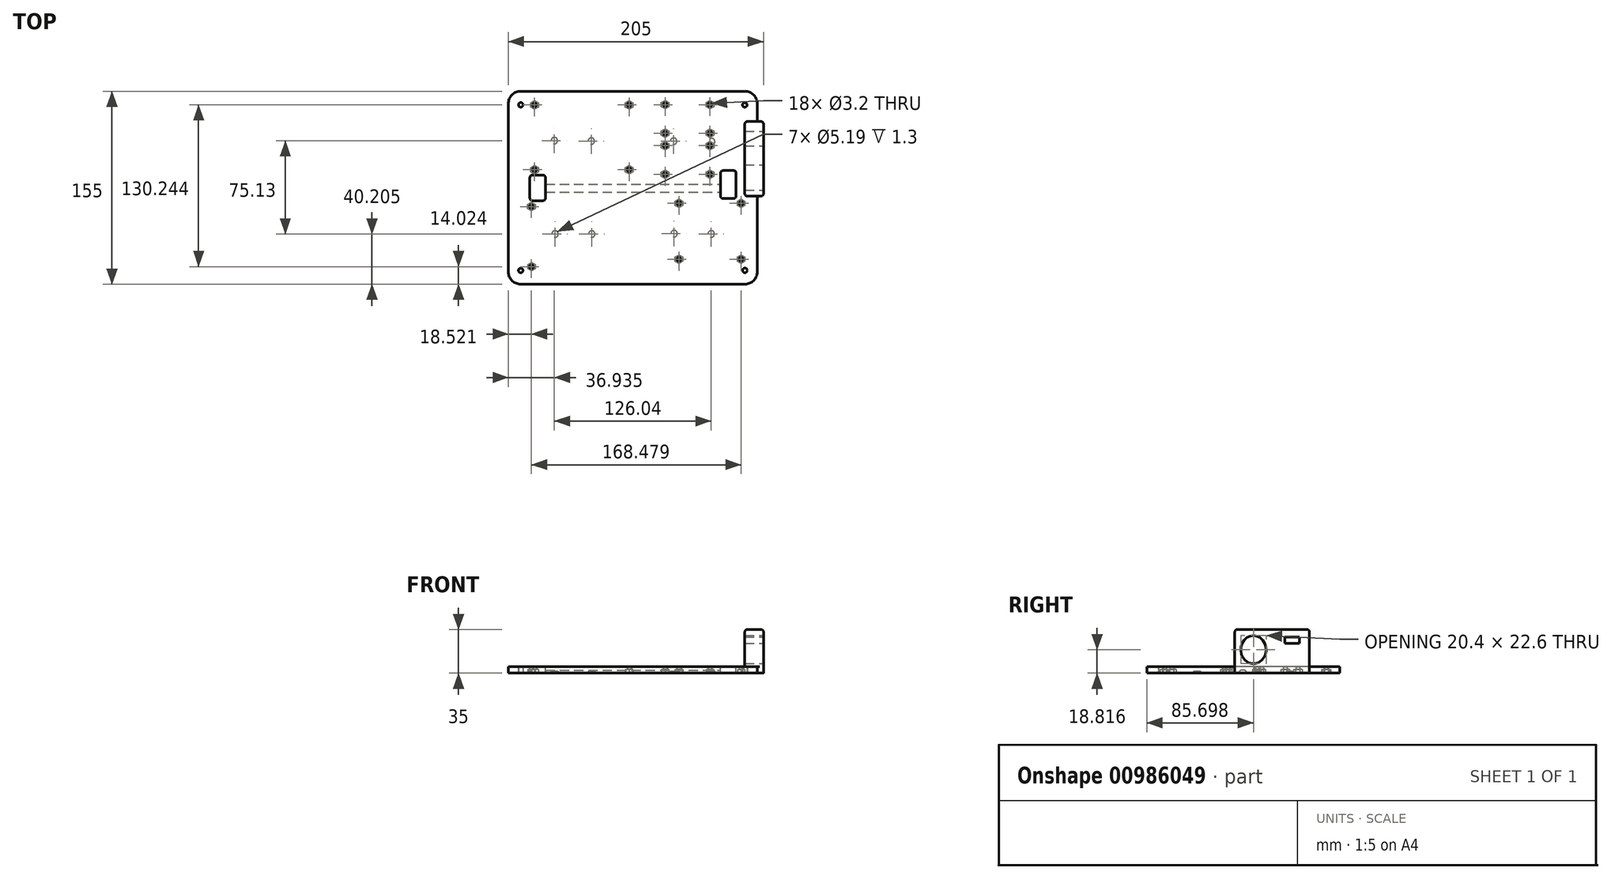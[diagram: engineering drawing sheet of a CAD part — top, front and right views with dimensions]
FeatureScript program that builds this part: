
annotation { "Feature Type Name" : "Feature", "Feature Type Description" : "" }
export const myFeature = defineFeature(function(context is Context, id is Id, definition is map)
    precondition{}
    {
        {
            var Q0;
            Q0=qCreatedBy(makeId("Top.planeOp"),FACE);
            var sketch = newSketch(context, id + "F0", { "sketchPlane" : qUnion([Q0])});
            skLineSegment(sketch, "E0.bottom", {"start": v(90, 77.5) * mm, "end": v(-90, 77.5) * mm});
            skLineSegment(sketch, "E0.top", {"start": v(90, -77.5) * mm, "end": v(-90, -77.5) * mm});
            skLineSegment(sketch, "E0.left", {"start": v(100, 67.5) * mm, "end": v(100, -67.5) * mm});
            skLineSegment(sketch, "E0.right", {"start": v(-100, 67.5) * mm, "end": v(-100, -67.5) * mm});
            skPoint(sketch, "E0.middle", {"position": v(0, 0) * mm});
            skPoint(sketch, "E1.visualSharp", {"position": v(-100, 77.5) * mm});
            skArc(sketch, "E1.filletArc", {"start": v(-90, 77.5) * mm, "mid": v(-97.07, 74.57) * mm, "end": v(-100, 67.5) * mm});
            skPoint(sketch, "E2.visualSharp", {"position": v(-100, -77.5) * mm});
            skArc(sketch, "E2.filletArc", {"start": v(-100, -67.5) * mm, "mid": v(-97.07, -74.57) * mm, "end": v(-90, -77.5) * mm});
            skPoint(sketch, "E3.visualSharp", {"position": v(100, -77.5) * mm});
            skArc(sketch, "E3.filletArc", {"start": v(90, -77.5) * mm, "mid": v(97.07, -74.57) * mm, "end": v(100, -67.5) * mm});
            skPoint(sketch, "E4.visualSharp", {"position": v(100, 77.5) * mm});
            skArc(sketch, "E4.filletArc", {"start": v(100, 67.5) * mm, "mid": v(97.07, 74.57) * mm, "end": v(90, 77.5) * mm});
            skSolve(sketch);
        }
        {
            var Q0;
            Q0=makeQuery(id+"F0.imprint","IMPRINT",FACE,{"disambiguationData":[TD([[makeQuery(id+"F0.imprint","IMPRINT",EDGE,{"derivedFrom":sQuery(id+"F0.wireOp",EDGE,"E0.bottom")}),1.0]])]});
            extrude(context, id + "F1", {"entities" : qUnion([Q0]), "depth" : 5 * mm, "offsetDistance" : 25 * mm});
        }
        {
            var Q0;
            Q0=qCreatedBy(makeId("Top.planeOp"),FACE);
            var sketch = newSketch(context, id + "F2", { "sketchPlane" : qUnion([Q0])});
            skCircle(sketch, "E5", {"center": v(-90.08, -66.5) * mm, "radius": 1.85 * mm});
            skCircle(sketch, "E6", {"center": v(90.07, -66.42) * mm, "radius": 1.85 * mm});
            skCircle(sketch, "E7", {"center": v(-90.05, 66.58) * mm, "radius": 1.85 * mm});
            skCircle(sketch, "E8", {"center": v(89.94, 66.51) * mm, "radius": 1.85 * mm});
            skCircle(sketch, "E9", {"center": v(-62.46, -37.16) * mm, "radius": 2.6 * mm});
            skCircle(sketch, "E10", {"center": v(-63.07, 37.84) * mm, "radius": 2.6 * mm});
            skCircle(sketch, "E11", {"center": v(-33.39, 37.49) * mm, "radius": 2.6 * mm});
            skCircle(sketch, "E12", {"center": v(32.78, 37.34) * mm, "radius": 2.6 * mm});
            skCircle(sketch, "E13", {"center": v(62.98, -37.14) * mm, "radius": 2.6 * mm});
            skCircle(sketch, "E14", {"center": v(33.16, -36.9) * mm, "radius": 2.6 * mm});
            skCircle(sketch, "E15", {"center": v(-32.97, -37.3) * mm, "radius": 2.6 * mm});
            skCircle(sketch, "E16", {"center": v(63.34, 37) * mm, "radius": 2.6 * mm});
            skLineSegment(sketch, "E17.bottom", {"start": v(-79.95, -3.5) * mm, "end": v(80.05, -3.5) * mm});
            skLineSegment(sketch, "E17.top", {"start": v(-79.95, 2.7) * mm, "end": v(80.05, 2.7) * mm});
            skLineSegment(sketch, "E17.left", {"start": v(-79.95, -3.5) * mm, "end": v(-79.95, 2.7) * mm});
            skLineSegment(sketch, "E17.right", {"start": v(80.05, -3.5) * mm, "end": v(80.05, 2.7) * mm});
            skLineSegment(sketch, "E18", {"start": v(-10.82, -3.5) * mm, "end": v(-10.82, -77.5) * mm});
            skLineSegment(sketch, "E19", {"start": v(-79.95, -1.61) * mm, "end": v(-99.95, -1.61) * mm});
            skSolve(sketch);
        }
        {
            var Q0;
            Q0=makeQuery(id+"F2.imprint","IMPRINT",FACE,{"disambiguationData":[TD([[makeQuery(id+"F2.imprint","IMPRINT",EDGE,{"derivedFrom":sQuery(id+"F2.wireOp",EDGE,"E5")}),1.0]])]});
            var Q1;
            Q1=makeQuery(id+"F2.imprint","IMPRINT",FACE,{"disambiguationData":[TD([[makeQuery(id+"F2.imprint","IMPRINT",EDGE,{"derivedFrom":sQuery(id+"F2.wireOp",EDGE,"E6")}),1.0]])]});
            var Q2;
            Q2=makeQuery(id+"F2.imprint","IMPRINT",FACE,{"disambiguationData":[TD([[makeQuery(id+"F2.imprint","IMPRINT",EDGE,{"derivedFrom":sQuery(id+"F2.wireOp",EDGE,"E7")}),1.0]])]});
            var Q3;
            Q3=makeQuery(id+"F2.imprint","IMPRINT",FACE,{"disambiguationData":[TD([[makeQuery(id+"F2.imprint","IMPRINT",EDGE,{"derivedFrom":sQuery(id+"F2.wireOp",EDGE,"E8")}),1.0]])]});
            extrude(context, id + "F3", {"entities" : qUnion([Q0, Q1, Q2, Q3]), "operationType" : NewBodyOperationType.REMOVE, "depth" : 5 * mm, "offsetDistance" : 25 * mm});
        }
        {
            var Q0;
            Q0=makeQuery(id+"F2.imprint","IMPRINT",FACE,{"disambiguationData":[TD([[makeQuery(id+"F2.imprint","IMPRINT",EDGE,{"derivedFrom":sQuery(id+"F2.wireOp",EDGE,"E9")}),1.0]])]});
            var Q1;
            Q1=makeQuery(id+"F2.imprint","IMPRINT",FACE,{"disambiguationData":[TD([[makeQuery(id+"F2.imprint","IMPRINT",EDGE,{"derivedFrom":sQuery(id+"F2.wireOp",EDGE,"E15")}),1.0]])]});
            var Q2;
            Q2=makeQuery(id+"F2.imprint","IMPRINT",FACE,{"disambiguationData":[TD([[makeQuery(id+"F2.imprint","IMPRINT",EDGE,{"derivedFrom":sQuery(id+"F2.wireOp",EDGE,"E14")}),1.0]])]});
            var Q3;
            Q3=makeQuery(id+"F2.imprint","IMPRINT",FACE,{"disambiguationData":[TD([[makeQuery(id+"F2.imprint","IMPRINT",EDGE,{"derivedFrom":sQuery(id+"F2.wireOp",EDGE,"E13")}),1.0]])]});
            var Q4;
            Q4=makeQuery(id+"F2.imprint","IMPRINT",FACE,{"disambiguationData":[TD([[makeQuery(id+"F2.imprint","IMPRINT",EDGE,{"derivedFrom":sQuery(id+"F2.wireOp",EDGE,"E16")}),1.0]])]});
            var Q5;
            Q5=makeQuery(id+"F2.imprint","IMPRINT",FACE,{"disambiguationData":[TD([[makeQuery(id+"F2.imprint","IMPRINT",EDGE,{"derivedFrom":sQuery(id+"F2.wireOp",EDGE,"E12")}),1.0]])]});
            var Q6;
            Q6=makeQuery(id+"F2.imprint","IMPRINT",FACE,{"disambiguationData":[TD([[makeQuery(id+"F2.imprint","IMPRINT",EDGE,{"derivedFrom":sQuery(id+"F2.wireOp",EDGE,"E11")}),1.0]])]});
            var Q7;
            Q7=makeQuery(id+"F2.imprint","IMPRINT",FACE,{"disambiguationData":[TD([[makeQuery(id+"F2.imprint","IMPRINT",EDGE,{"derivedFrom":sQuery(id+"F2.wireOp",EDGE,"E10")}),1.0]])]});
            extrude(context, id + "F4", {"entities" : qUnion([Q0, Q1, Q2, Q3, Q4, Q5, Q6, Q7]), "operationType" : NewBodyOperationType.REMOVE, "depth" : 1.3 * mm, "offsetDistance" : 25 * mm});
        }
        {
            var Q0;
            Q0=makeQuery(id+"F2.imprint","IMPRINT",FACE,{"disambiguationData":[TD([[makeQuery(id+"F2.imprint","IMPRINT",EDGE,{"derivedFrom":sQuery(id+"F2.wireOp",EDGE,"E17.bottom")}),1.0]])]});
            extrude(context, id + "F5", {"entities" : qUnion([Q0]), "operationType" : NewBodyOperationType.REMOVE, "depth" : 2.17 * mm, "offsetDistance" : 25 * mm});
        }
        {
            var Q0;
            Q0=qCreatedBy(makeId("Top.planeOp"),FACE);
            var sketch = newSketch(context, id + "F6", { "sketchPlane" : qUnion([Q0])});
            skCircle(sketch, "E20.cCircle", {"center": v(37, -57.5) * mm, "radius": 3 * mm, "construction": true});
            skLineSegment(sketch, "E20.0", {"start": v(40, -55.77) * mm, "end": v(40, -59.23) * mm});
            skLineSegment(sketch, "E20.1", {"start": v(40, -59.23) * mm, "end": v(37, -60.96) * mm});
            skLineSegment(sketch, "E20.2", {"start": v(37, -60.96) * mm, "end": v(34, -59.23) * mm});
            skLineSegment(sketch, "E20.3", {"start": v(34, -59.23) * mm, "end": v(34, -55.77) * mm});
            skLineSegment(sketch, "E20.4", {"start": v(34, -55.77) * mm, "end": v(37, -54.04) * mm});
            skLineSegment(sketch, "E20.5", {"start": v(37, -54.04) * mm, "end": v(40, -55.77) * mm});
            skPoint(sketch, "E20.0.midPoint", {"position": v(40, -57.5) * mm});
            skCircle(sketch, "E21", {"center": v(37, -57.5) * mm, "radius": 1.6 * mm});
            skCircle(sketch, "E22.0.1.0", {"center": v(37, -12.5) * mm, "radius": 1.6 * mm});
            skLineSegment(sketch, "E22.0.1.1", {"start": v(34, -10.77) * mm, "end": v(37, -9.04) * mm});
            skLineSegment(sketch, "E22.0.1.2", {"start": v(37, -9.04) * mm, "end": v(40, -10.77) * mm});
            skCircle(sketch, "E22.0.1.3", {"center": v(37, -12.5) * mm, "radius": 3 * mm, "construction": true});
            skLineSegment(sketch, "E22.0.1.4", {"start": v(40, -10.77) * mm, "end": v(40, -14.23) * mm});
            skLineSegment(sketch, "E22.0.1.5", {"start": v(34, -14.23) * mm, "end": v(34, -10.77) * mm});
            skLineSegment(sketch, "E22.0.1.6", {"start": v(37, -15.96) * mm, "end": v(34, -14.23) * mm});
            skPoint(sketch, "E22.0.1.7", {"position": v(40, -12.5) * mm});
            skLineSegment(sketch, "E22.0.1.8", {"start": v(40, -14.23) * mm, "end": v(37, -15.96) * mm});
            skCircle(sketch, "E22.1.0.0", {"center": v(87, -57.5) * mm, "radius": 1.6 * mm});
            skLineSegment(sketch, "E22.1.0.1", {"start": v(84, -55.77) * mm, "end": v(87, -54.04) * mm});
            skLineSegment(sketch, "E22.1.0.2", {"start": v(87, -54.04) * mm, "end": v(90, -55.77) * mm});
            skCircle(sketch, "E22.1.0.3", {"center": v(87, -57.5) * mm, "radius": 3 * mm, "construction": true});
            skLineSegment(sketch, "E22.1.0.4", {"start": v(90, -55.77) * mm, "end": v(90, -59.23) * mm});
            skLineSegment(sketch, "E22.1.0.5", {"start": v(84, -59.23) * mm, "end": v(84, -55.77) * mm});
            skLineSegment(sketch, "E22.1.0.6", {"start": v(87, -60.96) * mm, "end": v(84, -59.23) * mm});
            skPoint(sketch, "E22.1.0.7", {"position": v(90, -57.5) * mm});
            skLineSegment(sketch, "E22.1.0.8", {"start": v(90, -59.23) * mm, "end": v(87, -60.96) * mm});
            skCircle(sketch, "E22.1.1.0", {"center": v(87, -12.5) * mm, "radius": 1.6 * mm});
            skLineSegment(sketch, "E22.1.1.1", {"start": v(84, -10.77) * mm, "end": v(87, -9.04) * mm});
            skLineSegment(sketch, "E22.1.1.2", {"start": v(87, -9.04) * mm, "end": v(90, -10.77) * mm});
            skCircle(sketch, "E22.1.1.3", {"center": v(87, -12.5) * mm, "radius": 3 * mm, "construction": true});
            skLineSegment(sketch, "E22.1.1.4", {"start": v(90, -10.77) * mm, "end": v(90, -14.23) * mm});
            skLineSegment(sketch, "E22.1.1.5", {"start": v(84, -14.23) * mm, "end": v(84, -10.77) * mm});
            skLineSegment(sketch, "E22.1.1.6", {"start": v(87, -15.96) * mm, "end": v(84, -14.23) * mm});
            skPoint(sketch, "E22.1.1.7", {"position": v(90, -12.5) * mm});
            skLineSegment(sketch, "E22.1.1.8", {"start": v(90, -14.23) * mm, "end": v(87, -15.96) * mm});
            skLineSegment(sketch, "E22.direction1", {"start": v(34, -59.23) * mm, "end": v(84, -59.23) * mm, "construction": true});
            skLineSegment(sketch, "E22.direction2", {"start": v(34, -59.23) * mm, "end": v(34, -14.23) * mm, "construction": true});
            skCircle(sketch, "E23.cCircle", {"center": v(26, 10.77) * mm, "radius": 3 * mm, "construction": true});
            skLineSegment(sketch, "E23.0", {"start": v(29, 12.5) * mm, "end": v(29, 9.04) * mm});
            skLineSegment(sketch, "E23.1", {"start": v(29, 9.04) * mm, "end": v(26, 7.3) * mm});
            skLineSegment(sketch, "E23.2", {"start": v(26, 7.3) * mm, "end": v(23, 9.04) * mm});
            skLineSegment(sketch, "E23.3", {"start": v(23, 9.04) * mm, "end": v(23, 12.5) * mm});
            skLineSegment(sketch, "E23.4", {"start": v(23, 12.5) * mm, "end": v(26, 14.23) * mm});
            skLineSegment(sketch, "E23.5", {"start": v(26, 14.23) * mm, "end": v(29, 12.5) * mm});
            skPoint(sketch, "E23.0.midPoint", {"position": v(29, 10.77) * mm});
            skCircle(sketch, "E24", {"center": v(26, 10.77) * mm, "radius": 1.6 * mm});
            skCircle(sketch, "E25.0.1.0", {"center": v(26, 33.77) * mm, "radius": 1.6 * mm});
            skLineSegment(sketch, "E25.0.1.1", {"start": v(23, 35.5) * mm, "end": v(26, 37.23) * mm});
            skLineSegment(sketch, "E25.0.1.2", {"start": v(26, 37.23) * mm, "end": v(29, 35.5) * mm});
            skCircle(sketch, "E25.0.1.3", {"center": v(26, 33.77) * mm, "radius": 3 * mm, "construction": true});
            skLineSegment(sketch, "E25.0.1.4", {"start": v(29, 35.5) * mm, "end": v(29, 32.04) * mm});
            skLineSegment(sketch, "E25.0.1.5", {"start": v(23, 32.04) * mm, "end": v(23, 35.5) * mm});
            skLineSegment(sketch, "E25.0.1.6", {"start": v(26, 30.3) * mm, "end": v(23, 32.04) * mm});
            skPoint(sketch, "E25.0.1.7", {"position": v(29, 33.77) * mm});
            skLineSegment(sketch, "E25.0.1.8", {"start": v(29, 32.04) * mm, "end": v(26, 30.3) * mm});
            skCircle(sketch, "E25.1.0.0", {"center": v(62, 10.77) * mm, "radius": 1.6 * mm});
            skLineSegment(sketch, "E25.1.0.1", {"start": v(59, 12.5) * mm, "end": v(62, 14.23) * mm});
            skLineSegment(sketch, "E25.1.0.2", {"start": v(62, 14.23) * mm, "end": v(65, 12.5) * mm});
            skCircle(sketch, "E25.1.0.3", {"center": v(62, 10.77) * mm, "radius": 3 * mm, "construction": true});
            skLineSegment(sketch, "E25.1.0.4", {"start": v(65, 12.5) * mm, "end": v(65, 9.04) * mm});
            skLineSegment(sketch, "E25.1.0.5", {"start": v(59, 9.04) * mm, "end": v(59, 12.5) * mm});
            skLineSegment(sketch, "E25.1.0.6", {"start": v(62, 7.3) * mm, "end": v(59, 9.04) * mm});
            skPoint(sketch, "E25.1.0.7", {"position": v(65, 10.77) * mm});
            skLineSegment(sketch, "E25.1.0.8", {"start": v(65, 9.04) * mm, "end": v(62, 7.3) * mm});
            skCircle(sketch, "E25.1.1.0", {"center": v(62, 33.77) * mm, "radius": 1.6 * mm});
            skLineSegment(sketch, "E25.1.1.1", {"start": v(59, 35.5) * mm, "end": v(62, 37.23) * mm});
            skLineSegment(sketch, "E25.1.1.2", {"start": v(62, 37.23) * mm, "end": v(65, 35.5) * mm});
            skCircle(sketch, "E25.1.1.3", {"center": v(62, 33.77) * mm, "radius": 3 * mm, "construction": true});
            skLineSegment(sketch, "E25.1.1.4", {"start": v(65, 35.5) * mm, "end": v(65, 32.04) * mm});
            skLineSegment(sketch, "E25.1.1.5", {"start": v(59, 32.04) * mm, "end": v(59, 35.5) * mm});
            skLineSegment(sketch, "E25.1.1.6", {"start": v(62, 30.3) * mm, "end": v(59, 32.04) * mm});
            skPoint(sketch, "E25.1.1.7", {"position": v(65, 33.77) * mm});
            skLineSegment(sketch, "E25.1.1.8", {"start": v(65, 32.04) * mm, "end": v(62, 30.3) * mm});
            skLineSegment(sketch, "E25.direction1", {"start": v(23, 9.04) * mm, "end": v(59, 9.04) * mm, "construction": true});
            skLineSegment(sketch, "E25.direction2", {"start": v(23, 9.04) * mm, "end": v(23, 32.04) * mm, "construction": true});
            skCircle(sketch, "E26.cCircle", {"center": v(26, 43.77) * mm, "radius": 3 * mm, "construction": true});
            skLineSegment(sketch, "E26.0", {"start": v(29, 45.5) * mm, "end": v(29, 42.04) * mm});
            skLineSegment(sketch, "E26.1", {"start": v(29, 42.04) * mm, "end": v(26, 40.3) * mm});
            skLineSegment(sketch, "E26.2", {"start": v(26, 40.3) * mm, "end": v(23, 42.04) * mm});
            skLineSegment(sketch, "E26.3", {"start": v(23, 42.04) * mm, "end": v(23, 45.5) * mm});
            skLineSegment(sketch, "E26.4", {"start": v(23, 45.5) * mm, "end": v(26, 47.23) * mm});
            skLineSegment(sketch, "E26.5", {"start": v(26, 47.23) * mm, "end": v(29, 45.5) * mm});
            skPoint(sketch, "E26.0.midPoint", {"position": v(29, 43.77) * mm});
            skCircle(sketch, "E27", {"center": v(26, 43.77) * mm, "radius": 1.6 * mm});
            skCircle(sketch, "E28.0.1.0", {"center": v(26, 66.77) * mm, "radius": 1.6 * mm});
            skLineSegment(sketch, "E28.0.1.1", {"start": v(23, 68.5) * mm, "end": v(26, 70.23) * mm});
            skLineSegment(sketch, "E28.0.1.2", {"start": v(26, 70.23) * mm, "end": v(29, 68.5) * mm});
            skCircle(sketch, "E28.0.1.3", {"center": v(26, 66.77) * mm, "radius": 3 * mm, "construction": true});
            skLineSegment(sketch, "E28.0.1.4", {"start": v(29, 68.5) * mm, "end": v(29, 65.04) * mm});
            skLineSegment(sketch, "E28.0.1.5", {"start": v(23, 65.04) * mm, "end": v(23, 68.5) * mm});
            skLineSegment(sketch, "E28.0.1.6", {"start": v(26, 63.3) * mm, "end": v(23, 65.04) * mm});
            skPoint(sketch, "E28.0.1.7", {"position": v(29, 66.77) * mm});
            skLineSegment(sketch, "E28.0.1.8", {"start": v(29, 65.04) * mm, "end": v(26, 63.3) * mm});
            skCircle(sketch, "E28.1.0.0", {"center": v(62, 43.77) * mm, "radius": 1.6 * mm});
            skLineSegment(sketch, "E28.1.0.1", {"start": v(59, 45.5) * mm, "end": v(62, 47.23) * mm});
            skLineSegment(sketch, "E28.1.0.2", {"start": v(62, 47.23) * mm, "end": v(65, 45.5) * mm});
            skCircle(sketch, "E28.1.0.3", {"center": v(62, 43.77) * mm, "radius": 3 * mm, "construction": true});
            skLineSegment(sketch, "E28.1.0.4", {"start": v(65, 45.5) * mm, "end": v(65, 42.04) * mm});
            skLineSegment(sketch, "E28.1.0.5", {"start": v(59, 42.04) * mm, "end": v(59, 45.5) * mm});
            skLineSegment(sketch, "E28.1.0.6", {"start": v(62, 40.3) * mm, "end": v(59, 42.04) * mm});
            skPoint(sketch, "E28.1.0.7", {"position": v(65, 43.77) * mm});
            skLineSegment(sketch, "E28.1.0.8", {"start": v(65, 42.04) * mm, "end": v(62, 40.3) * mm});
            skCircle(sketch, "E28.1.1.0", {"center": v(62, 66.77) * mm, "radius": 1.6 * mm});
            skLineSegment(sketch, "E28.1.1.1", {"start": v(59, 68.5) * mm, "end": v(62, 70.23) * mm});
            skLineSegment(sketch, "E28.1.1.2", {"start": v(62, 70.23) * mm, "end": v(65, 68.5) * mm});
            skCircle(sketch, "E28.1.1.3", {"center": v(62, 66.77) * mm, "radius": 3 * mm, "construction": true});
            skLineSegment(sketch, "E28.1.1.4", {"start": v(65, 68.5) * mm, "end": v(65, 65.04) * mm});
            skLineSegment(sketch, "E28.1.1.5", {"start": v(59, 65.04) * mm, "end": v(59, 68.5) * mm});
            skLineSegment(sketch, "E28.1.1.6", {"start": v(62, 63.3) * mm, "end": v(59, 65.04) * mm});
            skPoint(sketch, "E28.1.1.7", {"position": v(65, 66.77) * mm});
            skLineSegment(sketch, "E28.1.1.8", {"start": v(65, 65.04) * mm, "end": v(62, 63.3) * mm});
            skLineSegment(sketch, "E28.direction1", {"start": v(23, 42.04) * mm, "end": v(59, 42.04) * mm, "construction": true});
            skLineSegment(sketch, "E28.direction2", {"start": v(23, 42.04) * mm, "end": v(23, 65.04) * mm, "construction": true});
            skCircle(sketch, "E29.1.1.0", {"center": v(-81.48, -15.15) * mm, "radius": 1.6 * mm});
            skLineSegment(sketch, "E29.1.1.1", {"start": v(-84.38, -13.48) * mm, "end": v(-81.48, -11.8) * mm});
            skLineSegment(sketch, "E29.1.1.2", {"start": v(-81.48, -11.8) * mm, "end": v(-78.58, -13.48) * mm});
            skCircle(sketch, "E29.1.1.3", {"center": v(-81.48, -15.15) * mm, "radius": 3 * mm, "construction": true});
            skLineSegment(sketch, "E29.1.1.4", {"start": v(-78.58, -13.48) * mm, "end": v(-78.58, -16.82) * mm});
            skLineSegment(sketch, "E29.1.1.5", {"start": v(-84.38, -16.82) * mm, "end": v(-84.38, -13.48) * mm});
            skLineSegment(sketch, "E29.1.1.6", {"start": v(-81.48, -18.5) * mm, "end": v(-84.38, -16.82) * mm});
            skPoint(sketch, "E29.1.1.7", {"position": v(-78.58, -15.15) * mm});
            skLineSegment(sketch, "E29.1.1.8", {"start": v(-78.58, -16.82) * mm, "end": v(-81.48, -18.5) * mm});
            skCircle(sketch, "E30.1.1.0", {"center": v(-81.48, -63.48) * mm, "radius": 1.6 * mm});
            skLineSegment(sketch, "E30.1.1.1", {"start": v(-84.29, -61.8) * mm, "end": v(-81.39, -60.13) * mm});
            skLineSegment(sketch, "E30.1.1.2", {"start": v(-81.39, -60.13) * mm, "end": v(-78.49, -61.8) * mm});
            skCircle(sketch, "E30.1.1.3", {"center": v(-81.48, -63.48) * mm, "radius": 3 * mm, "construction": true});
            skLineSegment(sketch, "E30.1.1.4", {"start": v(-78.49, -61.8) * mm, "end": v(-78.49, -65.15) * mm});
            skLineSegment(sketch, "E30.1.1.5", {"start": v(-84.29, -65.15) * mm, "end": v(-84.29, -61.8) * mm});
            skLineSegment(sketch, "E30.1.1.6", {"start": v(-81.39, -66.82) * mm, "end": v(-84.29, -65.15) * mm});
            skPoint(sketch, "E30.1.1.7", {"position": v(-78.49, -63.48) * mm});
            skLineSegment(sketch, "E30.1.1.8", {"start": v(-78.49, -65.15) * mm, "end": v(-81.39, -66.82) * mm});
            skCircle(sketch, "E31.cCircle", {"center": v(-79, 14.5) * mm, "radius": 3 * mm, "construction": true});
            skLineSegment(sketch, "E31.0", {"start": v(-76, 16.23) * mm, "end": v(-76, 12.77) * mm});
            skLineSegment(sketch, "E31.1", {"start": v(-76, 12.77) * mm, "end": v(-79, 11.04) * mm});
            skLineSegment(sketch, "E31.2", {"start": v(-79, 11.04) * mm, "end": v(-82, 12.77) * mm});
            skLineSegment(sketch, "E31.3", {"start": v(-82, 12.77) * mm, "end": v(-82, 16.23) * mm});
            skLineSegment(sketch, "E31.4", {"start": v(-82, 16.23) * mm, "end": v(-79, 17.96) * mm});
            skLineSegment(sketch, "E31.5", {"start": v(-79, 17.96) * mm, "end": v(-76, 16.23) * mm});
            skPoint(sketch, "E31.0.midPoint", {"position": v(-76, 14.5) * mm});
            skCircle(sketch, "E32", {"center": v(-79, 14.5) * mm, "radius": 1.6 * mm});
            skCircle(sketch, "E33.0.1.0", {"center": v(-79, 66.5) * mm, "radius": 1.6 * mm});
            skLineSegment(sketch, "E33.0.1.1", {"start": v(-82, 68.23) * mm, "end": v(-79, 69.96) * mm});
            skLineSegment(sketch, "E33.0.1.2", {"start": v(-79, 69.96) * mm, "end": v(-76, 68.23) * mm});
            skCircle(sketch, "E33.0.1.3", {"center": v(-79, 66.5) * mm, "radius": 3 * mm, "construction": true});
            skLineSegment(sketch, "E33.0.1.4", {"start": v(-76, 68.23) * mm, "end": v(-76, 64.77) * mm});
            skLineSegment(sketch, "E33.0.1.5", {"start": v(-82, 64.77) * mm, "end": v(-82, 68.23) * mm});
            skLineSegment(sketch, "E33.0.1.6", {"start": v(-79, 63.04) * mm, "end": v(-82, 64.77) * mm});
            skPoint(sketch, "E33.0.1.7", {"position": v(-76, 66.5) * mm});
            skLineSegment(sketch, "E33.0.1.8", {"start": v(-76, 64.77) * mm, "end": v(-79, 63.04) * mm});
            skCircle(sketch, "E33.1.0.0", {"center": v(-3, 14.5) * mm, "radius": 1.6 * mm});
            skLineSegment(sketch, "E33.1.0.1", {"start": v(-6, 16.23) * mm, "end": v(-3, 17.96) * mm});
            skLineSegment(sketch, "E33.1.0.2", {"start": v(-3, 17.96) * mm, "end": v(0, 16.23) * mm});
            skCircle(sketch, "E33.1.0.3", {"center": v(-3, 14.5) * mm, "radius": 3 * mm, "construction": true});
            skLineSegment(sketch, "E33.1.0.4", {"start": v(0, 16.23) * mm, "end": v(0, 12.77) * mm});
            skLineSegment(sketch, "E33.1.0.5", {"start": v(-6, 12.77) * mm, "end": v(-6, 16.23) * mm});
            skLineSegment(sketch, "E33.1.0.6", {"start": v(-3, 11.04) * mm, "end": v(-6, 12.77) * mm});
            skPoint(sketch, "E33.1.0.7", {"position": v(0, 14.5) * mm});
            skLineSegment(sketch, "E33.1.0.8", {"start": v(0, 12.77) * mm, "end": v(-3, 11.04) * mm});
            skCircle(sketch, "E33.1.1.0", {"center": v(-3, 66.5) * mm, "radius": 1.6 * mm});
            skLineSegment(sketch, "E33.1.1.1", {"start": v(-6, 68.23) * mm, "end": v(-3, 69.96) * mm});
            skLineSegment(sketch, "E33.1.1.2", {"start": v(-3, 69.96) * mm, "end": v(0, 68.23) * mm});
            skCircle(sketch, "E33.1.1.3", {"center": v(-3, 66.5) * mm, "radius": 3 * mm, "construction": true});
            skLineSegment(sketch, "E33.1.1.4", {"start": v(0, 68.23) * mm, "end": v(0, 64.77) * mm});
            skLineSegment(sketch, "E33.1.1.5", {"start": v(-6, 64.77) * mm, "end": v(-6, 68.23) * mm});
            skLineSegment(sketch, "E33.1.1.6", {"start": v(-3, 63.04) * mm, "end": v(-6, 64.77) * mm});
            skPoint(sketch, "E33.1.1.7", {"position": v(0, 66.5) * mm});
            skLineSegment(sketch, "E33.1.1.8", {"start": v(0, 64.77) * mm, "end": v(-3, 63.04) * mm});
            skLineSegment(sketch, "E33.direction1", {"start": v(-82, 12.77) * mm, "end": v(-6, 12.77) * mm, "construction": true});
            skLineSegment(sketch, "E33.direction2", {"start": v(-82, 12.77) * mm, "end": v(-82, 64.77) * mm, "construction": true});
            skSolve(sketch);
        }
        {
            var Q0;
            Q0=makeQuery(id+"F6.imprint","IMPRINT",FACE,{"disambiguationData":[TD([[makeQuery(id+"F6.imprint","IMPRINT",EDGE,{"derivedFrom":sQuery(id+"F6.wireOp",EDGE,"E25.0.1.0")}),-1.0]])]});
            var Q1;
            Q1=makeQuery(id+"F6.imprint","IMPRINT",FACE,{"disambiguationData":[TD([[makeQuery(id+"F6.imprint","IMPRINT",EDGE,{"derivedFrom":sQuery(id+"F6.wireOp",EDGE,"E26.0")}),-1.0]])]});
            var Q2;
            Q2=makeQuery(id+"F6.imprint","IMPRINT",FACE,{"disambiguationData":[TD([[makeQuery(id+"F6.imprint","IMPRINT",EDGE,{"derivedFrom":sQuery(id+"F6.wireOp",EDGE,"E28.1.0.0")}),-1.0]])]});
            var Q3;
            Q3=makeQuery(id+"F6.imprint","IMPRINT",FACE,{"disambiguationData":[TD([[makeQuery(id+"F6.imprint","IMPRINT",EDGE,{"derivedFrom":sQuery(id+"F6.wireOp",EDGE,"E25.1.1.0")}),-1.0]])]});
            var Q4;
            Q4=makeQuery(id+"F6.imprint","IMPRINT",FACE,{"disambiguationData":[TD([[makeQuery(id+"F6.imprint","IMPRINT",EDGE,{"derivedFrom":sQuery(id+"F6.wireOp",EDGE,"E28.0.1.0")}),-1.0]])]});
            var Q5;
            Q5=makeQuery(id+"F6.imprint","IMPRINT",FACE,{"disambiguationData":[TD([[makeQuery(id+"F6.imprint","IMPRINT",EDGE,{"derivedFrom":sQuery(id+"F6.wireOp",EDGE,"E28.1.1.0")}),-1.0]])]});
            var Q6;
            Q6=makeQuery(id+"F6.imprint","IMPRINT",FACE,{"disambiguationData":[TD([[makeQuery(id+"F6.imprint","IMPRINT",EDGE,{"derivedFrom":sQuery(id+"F6.wireOp",EDGE,"E33.1.0.0")}),-1.0]])]});
            var Q7;
            Q7=makeQuery(id+"F6.imprint","IMPRINT",FACE,{"disambiguationData":[TD([[makeQuery(id+"F6.imprint","IMPRINT",EDGE,{"derivedFrom":sQuery(id+"F6.wireOp",EDGE,"E31.0")}),-1.0]])]});
            var Q8;
            Q8=makeQuery(id+"F6.imprint","IMPRINT",FACE,{"disambiguationData":[TD([[makeQuery(id+"F6.imprint","IMPRINT",EDGE,{"derivedFrom":sQuery(id+"F6.wireOp",EDGE,"E33.0.1.0")}),-1.0]])]});
            var Q9;
            Q9=makeQuery(id+"F6.imprint","IMPRINT",FACE,{"disambiguationData":[TD([[makeQuery(id+"F6.imprint","IMPRINT",EDGE,{"derivedFrom":sQuery(id+"F6.wireOp",EDGE,"E30.1.1.0")}),-1.0]])]});
            var Q10;
            Q10=makeQuery(id+"F6.imprint","IMPRINT",FACE,{"disambiguationData":[TD([[makeQuery(id+"F6.imprint","IMPRINT",EDGE,{"derivedFrom":sQuery(id+"F6.wireOp",EDGE,"E29.1.1.0")}),-1.0]])]});
            var Q11;
            Q11=makeQuery(id+"F6.imprint","IMPRINT",FACE,{"disambiguationData":[TD([[makeQuery(id+"F6.imprint","IMPRINT",EDGE,{"derivedFrom":sQuery(id+"F6.wireOp",EDGE,"E22.1.0.0")}),-1.0]])]});
            var Q12;
            Q12=makeQuery(id+"F6.imprint","IMPRINT",FACE,{"disambiguationData":[TD([[makeQuery(id+"F6.imprint","IMPRINT",EDGE,{"derivedFrom":sQuery(id+"F6.wireOp",EDGE,"E20.0")}),-1.0]])]});
            var Q13;
            Q13=makeQuery(id+"F6.imprint","IMPRINT",FACE,{"disambiguationData":[TD([[makeQuery(id+"F6.imprint","IMPRINT",EDGE,{"derivedFrom":sQuery(id+"F6.wireOp",EDGE,"E22.0.1.0")}),-1.0]])]});
            var Q14;
            Q14=makeQuery(id+"F6.imprint","IMPRINT",FACE,{"disambiguationData":[TD([[makeQuery(id+"F6.imprint","IMPRINT",EDGE,{"derivedFrom":sQuery(id+"F6.wireOp",EDGE,"E22.1.1.0")}),-1.0]])]});
            var Q15;
            Q15=makeQuery(id+"F6.imprint","IMPRINT",FACE,{"disambiguationData":[TD([[makeQuery(id+"F6.imprint","IMPRINT",EDGE,{"derivedFrom":sQuery(id+"F6.wireOp",EDGE,"E23.0")}),-1.0]])]});
            var Q16;
            Q16=makeQuery(id+"F6.imprint","IMPRINT",FACE,{"disambiguationData":[TD([[makeQuery(id+"F6.imprint","IMPRINT",EDGE,{"derivedFrom":sQuery(id+"F6.wireOp",EDGE,"E33.1.1.0")}),-1.0]])]});
            var Q17;
            Q17=makeQuery(id+"F6.imprint","IMPRINT",FACE,{"disambiguationData":[TD([[makeQuery(id+"F6.imprint","IMPRINT",EDGE,{"derivedFrom":sQuery(id+"F6.wireOp",EDGE,"E25.1.0.0")}),-1.0]])]});
            extrude(context, id + "F7", {"entities" : qUnion([Q0, Q1, Q2, Q3, Q4, Q5, Q6, Q7, Q8, Q9, Q10, Q11, Q12, Q13, Q14, Q15, Q16, Q17]), "operationType" : NewBodyOperationType.REMOVE, "depth" : 3 * mm, "offsetDistance" : 25 * mm});
        }
        {
            var Q0;
            Q0=makeQuery(id+"F6.imprint","IMPRINT",FACE,{"disambiguationData":[TD([[makeQuery(id+"F6.imprint","IMPRINT",EDGE,{"derivedFrom":sQuery(id+"F6.wireOp",EDGE,"E24")}),1.0]])]});
            var Q1;
            Q1=makeQuery(id+"F6.imprint","IMPRINT",FACE,{"disambiguationData":[TD([[makeQuery(id+"F6.imprint","IMPRINT",EDGE,{"derivedFrom":sQuery(id+"F6.wireOp",EDGE,"E22.0.1.0")}),1.0]])]});
            var Q2;
            Q2=makeQuery(id+"F6.imprint","IMPRINT",FACE,{"disambiguationData":[TD([[makeQuery(id+"F6.imprint","IMPRINT",EDGE,{"derivedFrom":sQuery(id+"F6.wireOp",EDGE,"E25.0.1.0")}),1.0]])]});
            var Q3;
            Q3=makeQuery(id+"F6.imprint","IMPRINT",FACE,{"disambiguationData":[TD([[makeQuery(id+"F6.imprint","IMPRINT",EDGE,{"derivedFrom":sQuery(id+"F6.wireOp",EDGE,"E27")}),1.0]])]});
            var Q4;
            Q4=makeQuery(id+"F6.imprint","IMPRINT",FACE,{"disambiguationData":[TD([[makeQuery(id+"F6.imprint","IMPRINT",EDGE,{"derivedFrom":sQuery(id+"F6.wireOp",EDGE,"E28.0.1.0")}),1.0]])]});
            var Q5;
            Q5=makeQuery(id+"F6.imprint","IMPRINT",FACE,{"disambiguationData":[TD([[makeQuery(id+"F6.imprint","IMPRINT",EDGE,{"derivedFrom":sQuery(id+"F6.wireOp",EDGE,"E28.1.1.0")}),1.0]])]});
            var Q6;
            Q6=makeQuery(id+"F6.imprint","IMPRINT",FACE,{"disambiguationData":[TD([[makeQuery(id+"F6.imprint","IMPRINT",EDGE,{"derivedFrom":sQuery(id+"F6.wireOp",EDGE,"E28.1.0.0")}),1.0]])]});
            var Q7;
            Q7=makeQuery(id+"F6.imprint","IMPRINT",FACE,{"disambiguationData":[TD([[makeQuery(id+"F6.imprint","IMPRINT",EDGE,{"derivedFrom":sQuery(id+"F6.wireOp",EDGE,"E25.1.1.0")}),1.0]])]});
            var Q8;
            Q8=makeQuery(id+"F6.imprint","IMPRINT",FACE,{"disambiguationData":[TD([[makeQuery(id+"F6.imprint","IMPRINT",EDGE,{"derivedFrom":sQuery(id+"F6.wireOp",EDGE,"E22.1.1.0")}),1.0]])]});
            var Q9;
            Q9=makeQuery(id+"F6.imprint","IMPRINT",FACE,{"disambiguationData":[TD([[makeQuery(id+"F6.imprint","IMPRINT",EDGE,{"derivedFrom":sQuery(id+"F6.wireOp",EDGE,"E22.1.0.0")}),1.0]])]});
            var Q10;
            Q10=makeQuery(id+"F6.imprint","IMPRINT",FACE,{"disambiguationData":[TD([[makeQuery(id+"F6.imprint","IMPRINT",EDGE,{"derivedFrom":sQuery(id+"F6.wireOp",EDGE,"E21")}),1.0]])]});
            var Q11;
            Q11=makeQuery(id+"F6.imprint","IMPRINT",FACE,{"disambiguationData":[TD([[makeQuery(id+"F6.imprint","IMPRINT",EDGE,{"derivedFrom":sQuery(id+"F6.wireOp",EDGE,"E30.1.1.0")}),1.0]])]});
            var Q12;
            Q12=makeQuery(id+"F6.imprint","IMPRINT",FACE,{"disambiguationData":[TD([[makeQuery(id+"F6.imprint","IMPRINT",EDGE,{"derivedFrom":sQuery(id+"F6.wireOp",EDGE,"E29.1.1.0")}),1.0]])]});
            var Q13;
            Q13=makeQuery(id+"F6.imprint","IMPRINT",FACE,{"disambiguationData":[TD([[makeQuery(id+"F6.imprint","IMPRINT",EDGE,{"derivedFrom":sQuery(id+"F6.wireOp",EDGE,"E32")}),1.0]])]});
            var Q14;
            Q14=makeQuery(id+"F6.imprint","IMPRINT",FACE,{"disambiguationData":[TD([[makeQuery(id+"F6.imprint","IMPRINT",EDGE,{"derivedFrom":sQuery(id+"F6.wireOp",EDGE,"E33.1.0.0")}),1.0]])]});
            var Q15;
            Q15=makeQuery(id+"F6.imprint","IMPRINT",FACE,{"disambiguationData":[TD([[makeQuery(id+"F6.imprint","IMPRINT",EDGE,{"derivedFrom":sQuery(id+"F6.wireOp",EDGE,"E33.1.1.0")}),1.0]])]});
            var Q16;
            Q16=makeQuery(id+"F6.imprint","IMPRINT",FACE,{"disambiguationData":[TD([[makeQuery(id+"F6.imprint","IMPRINT",EDGE,{"derivedFrom":sQuery(id+"F6.wireOp",EDGE,"E33.0.1.0")}),1.0]])]});
            var Q17;
            Q17=makeQuery(id+"F6.imprint","IMPRINT",FACE,{"disambiguationData":[TD([[makeQuery(id+"F6.imprint","IMPRINT",EDGE,{"derivedFrom":sQuery(id+"F6.wireOp",EDGE,"E25.1.0.0")}),1.0]])]});
            extrude(context, id + "F8", {"entities" : qUnion([Q0, Q1, Q2, Q3, Q4, Q5, Q6, Q7, Q8, Q9, Q10, Q11, Q12, Q13, Q14, Q15, Q16, Q17]), "operationType" : NewBodyOperationType.REMOVE, "depth" : 5 * mm, "offsetDistance" : 25 * mm});
        }
        {
            var Q0;
            Q0=makeQuery(id+"F1.opExtrude","CAP_FACE",FACE,{"disambiguationData":[OSD([sQuery(id+"F0.wireOp",EDGE,"E0.bottom"),sQuery(id+"F0.wireOp",EDGE,"E0.top"),sQuery(id+"F0.wireOp",EDGE,"E0.left"),sQuery(id+"F0.wireOp",EDGE,"E0.right"),sQuery(id+"F0.wireOp",EDGE,"E1.filletArc"),sQuery(id+"F0.wireOp",EDGE,"E2.filletArc"),sQuery(id+"F0.wireOp",EDGE,"E3.filletArc"),sQuery(id+"F0.wireOp",EDGE,"E4.filletArc")])],"isStart":false});
            var sketch = newSketch(context, id + "F9", { "sketchPlane" : qUnion([Q0])});
            skLineSegment(sketch, "E34.bottom", {"start": v(-82.7, 10.12) * mm, "end": v(-70.2, 10.12) * mm});
            skLineSegment(sketch, "E34.top", {"start": v(-82.7, -10.43) * mm, "end": v(-70.2, -10.43) * mm});
            skLineSegment(sketch, "E34.left", {"start": v(-82.7, 10.12) * mm, "end": v(-82.7, -10.43) * mm});
            skLineSegment(sketch, "E34.right", {"start": v(-70.2, 10.12) * mm, "end": v(-70.2, -10.43) * mm});
            skLineSegment(sketch, "E35.bottom", {"start": v(70.5, 13.78) * mm, "end": v(83, 13.78) * mm});
            skLineSegment(sketch, "E35.top", {"start": v(70.5, -8.72) * mm, "end": v(83, -8.72) * mm});
            skLineSegment(sketch, "E35.left", {"start": v(70.5, 13.78) * mm, "end": v(70.5, -8.72) * mm});
            skLineSegment(sketch, "E35.right", {"start": v(83, 13.78) * mm, "end": v(83, -8.72) * mm});
            skLineSegment(sketch, "E36.bottom", {"start": v(90, 53.2) * mm, "end": v(105, 53.2) * mm});
            skLineSegment(sketch, "E36.top", {"start": v(90, -6.8) * mm, "end": v(105, -6.8) * mm});
            skLineSegment(sketch, "E36.left", {"start": v(90, 53.2) * mm, "end": v(90, -6.8) * mm});
            skLineSegment(sketch, "E36.right", {"start": v(105, 53.2) * mm, "end": v(105, -6.8) * mm});
            skSolve(sketch);
        }
        {
            var Q0;
            Q0=makeQuery(id+"F9.imprint","IMPRINT",FACE,{"disambiguationData":[TD([[makeQuery(id+"F9.imprint","IMPRINT",EDGE,{"derivedFrom":sQuery(id+"F9.wireOp",EDGE,"E34.bottom")}),-1.0]])]});
            var Q1;
            Q1=makeQuery(id+"F9.imprint","IMPRINT",FACE,{"disambiguationData":[TD([[makeQuery(id+"F9.imprint","IMPRINT",EDGE,{"derivedFrom":sQuery(id+"F9.wireOp",EDGE,"E35.bottom")}),-1.0]])]});
            extrude(context, id + "F10", {"entities" : qUnion([Q0, Q1]), "operationType" : NewBodyOperationType.REMOVE, "oppositeDirection" : true, "depth" : 5 * mm, "offsetDistance" : 25 * mm});
        }
        {
            var Q0;
            {var subQ0=sQuery(id+"F9.wireOp",EDGE,"E36.left");Q0=makeQuery(id+"F9.imprint","IMPRINT",FACE,{"disambiguationData":[TD([[makeQuery(id+"F9.imprint","IMPRINT",EDGE,{"derivedFrom":subQ0}),1.0]])]});}
            var Q1;
            {var subQ0=sQuery(id+"F9.wireOp",EDGE,"E36.right");Q1=makeQuery(id+"F9.imprint","IMPRINT",FACE,{"disambiguationData":[TD([[makeQuery(id+"F9.imprint","IMPRINT",EDGE,{"derivedFrom":subQ0}),-1.0]])]});}
            extrude(context, id + "F11", {"entities" : qUnion([Q0, Q1]), "operationType" : NewBodyOperationType.ADD, "depth" : 30 * mm, "offsetDistance" : 25 * mm});
        }
        {
            var Q0;
            {var subQ0=sQuery(id+"F9.wireOp",EDGE,"E36.right");Q0=makeQuery(id+"F9.imprint","IMPRINT",FACE,{"disambiguationData":[TD([[makeQuery(id+"F9.imprint","IMPRINT",EDGE,{"derivedFrom":subQ0}),-1.0]])]});}
            extrude(context, id + "F12", {"entities" : qUnion([Q0]), "operationType" : NewBodyOperationType.ADD, "oppositeDirection" : true, "depth" : 5 * mm, "offsetDistance" : 25 * mm});
        }
        {
            var Q0;
            Q0=makeQuery(id+"FPu8u7fwWP3qDko_1.boolean.opBoolean","MERGE",FACE,{"derivedFrom":[makeQuery(id+"F1.opExtrude","SWEPT_FACE",FACE,{"disambiguationData":[OSD([sQuery(id+"F0.wireOp",EDGE,"E0.left")])]}),makeQuery(id+"FPu8u7fwWP3qDko_1.opExtrude","SWEPT_FACE",FACE,{"disambiguationData":[OSD([sQuery(id+"F9.wireOp",EDGE,"Owk9XRQi-8ec9-zV8l-TkBG-sjmoNjxYJclS.right")])]})]});
            var sketch = newSketch(context, id + "F13", { "sketchPlane" : qUnion([Q0])});
            skEllipse(sketch, "E37", {"center": v(8.2, 18.82) * mm, "majorRadius": 10.2 * mm, "minorRadius": 11.3 * mm, "majorAxis": v(1, 0)});
            skLineSegment(sketch, "E38.bottom", {"start": v(33.5, 29) * mm, "end": v(45.2, 29) * mm});
            skLineSegment(sketch, "E38.top", {"start": v(33.5, 23.7) * mm, "end": v(45.2, 23.7) * mm});
            skLineSegment(sketch, "E38.left", {"start": v(33.5, 29) * mm, "end": v(33.5, 23.7) * mm});
            skLineSegment(sketch, "E38.right", {"start": v(45.2, 29) * mm, "end": v(45.2, 23.7) * mm});
            skSolve(sketch);
        }
        {
            var Q0;
            {var subQ0=sQuery(id+"F13.wireOp",EDGE,"E37");var subQ1=sQuery(id+"F0.wireOp",EDGE,"E3.filletArc");var subQ2=sQuery(id+"F0.wireOp",EDGE,"E0.left");var subQ3=makeQuery(id+"FPu8u7fwWP3qDko_1.boolean.opBoolean","SPLIT",EDGE,{"disambiguationData":[TD([makeQuery(id+"F1.opExtrude","SWEPT_FACE",FACE,{"disambiguationData":[OSD([subQ1])]})])],"derivedFrom":makeQuery(id+"F1.opExtrude","CAP_EDGE",EDGE,{"disambiguationData":[OSD([subQ2])],"isStart":false})});var subQ4=makeQuery(id+"F13.imprint","INTERSECT",VERTEX,{"disambiguationData":[OD(0.0)],"derivedFrom":[subQ3,subQ0]});Q0=makeQuery(id+"F13.imprint","IMPRINT",FACE,{"disambiguationData":[TD([[makeQuery(id+"F13.imprint","IMPRINT",EDGE,{"disambiguationData":[TD([[subQ4,1.0]])],"derivedFrom":subQ0}),1.0]])]});}
            extrude(context, id + "F14", {"entities" : qUnion([Q0]), "operationType" : NewBodyOperationType.REMOVE, "oppositeDirection" : true, "depth" : 10 * mm, "offsetDistance" : 25 * mm});
        }
        {
            var Q0;
            {var subQ0=sQuery(id+"F13.wireOp",EDGE,"E37");var subQ1=sQuery(id+"F0.wireOp",EDGE,"E3.filletArc");var subQ2=sQuery(id+"F0.wireOp",EDGE,"E0.left");var subQ3=makeQuery(id+"FPu8u7fwWP3qDko_1.boolean.opBoolean","SPLIT",EDGE,{"disambiguationData":[TD([makeQuery(id+"F1.opExtrude","SWEPT_FACE",FACE,{"disambiguationData":[OSD([subQ1])]})])],"derivedFrom":makeQuery(id+"F1.opExtrude","CAP_EDGE",EDGE,{"disambiguationData":[OSD([subQ2])],"isStart":false})});var subQ4=makeQuery(id+"F13.imprint","INTERSECT",VERTEX,{"disambiguationData":[OD(0.0)],"derivedFrom":[subQ3,subQ0]});Q0=makeQuery(id+"F13.imprint","IMPRINT",FACE,{"disambiguationData":[TD([[makeQuery(id+"F13.imprint","IMPRINT",EDGE,{"disambiguationData":[TD([[subQ4,1.0]])],"derivedFrom":subQ0}),1.0]])]});}
            extrude(context, id + "F15", {"entities" : qUnion([Q0]), "operationType" : NewBodyOperationType.REMOVE, "depth" : 5 * mm, "offsetDistance" : 25 * mm});
        }
        {
            var Q0;
            Q0=makeQuery(id+"F13.imprint","IMPRINT",FACE,{"disambiguationData":[TD([[makeQuery(id+"F13.imprint","IMPRINT",EDGE,{"derivedFrom":sQuery(id+"F13.wireOp",EDGE,"E38.bottom")}),-1.0]])]});
            extrude(context, id + "F16", {"entities" : qUnion([Q0]), "operationType" : NewBodyOperationType.REMOVE, "oppositeDirection" : true, "depth" : 10 * mm, "offsetDistance" : 25 * mm});
        }
        {
            var Q0;
            Q0=makeQuery(id+"F13.imprint","IMPRINT",FACE,{"disambiguationData":[TD([[makeQuery(id+"F13.imprint","IMPRINT",EDGE,{"derivedFrom":sQuery(id+"F13.wireOp",EDGE,"E38.bottom")}),-1.0]])]});
            extrude(context, id + "F17", {"entities" : qUnion([Q0]), "operationType" : NewBodyOperationType.REMOVE, "depth" : 5 * mm, "offsetDistance" : 25 * mm});
        }
        {
            var Q0;
            Q0=makeQuery(id+"F5.boolean.opBoolean","COPY",EDGE,{"derivedFrom":makeQuery(id+"F5.opExtrude","CAP_EDGE",EDGE,{"disambiguationData":[OSD([sQuery(id+"F2.wireOp",EDGE,"E17.bottom")])],"isStart":false})});
            var Q1;
            Q1=makeQuery(id+"F5.boolean.opBoolean","COPY",EDGE,{"derivedFrom":makeQuery(id+"F5.opExtrude","CAP_EDGE",EDGE,{"disambiguationData":[OSD([sQuery(id+"F2.wireOp",EDGE,"E17.top")])],"isStart":false})});
            fillet(context, id + "F18", {"entities" : qUnion([Q0, Q1]), "radius" : 2 * mm, "tangentPropagation" : true, "allowEdgeOverflow" : false});
        }
        {
            var Q0;
            Q0=makeQuery(id+"F11.opExtrude","CAP_EDGE",EDGE,{"disambiguationData":[OSD([sQuery(id+"F9.wireOp",EDGE,"E36.top")])],"isStart":false});
            var Q1;
            Q1=makeQuery(id+"F11.opExtrude","CAP_EDGE",EDGE,{"disambiguationData":[OSD([sQuery(id+"F9.wireOp",EDGE,"E36.bottom")])],"isStart":false});
            var Q2;
            {var subQ0=sQuery(id+"F9.wireOp",EDGE,"E36.right");var subQ1=sQuery(id+"F9.wireOp",EDGE,"E36.top");Q2=makeQuery(id+"F12.boolean.opBoolean","MERGE",EDGE,{"derivedFrom":[makeQuery(id+"F11.opExtrude","SWEPT_EDGE",EDGE,{"disambiguationData":[OSD([subQ1,subQ0])]}),makeQuery(id+"F12.opExtrude","SWEPT_EDGE",EDGE,{"disambiguationData":[OSD([subQ1,subQ0])]})]});}
            var Q3;
            {var subQ0=sQuery(id+"F9.wireOp",EDGE,"E36.right");var subQ1=sQuery(id+"F9.wireOp",EDGE,"E36.bottom");Q3=makeQuery(id+"F12.boolean.opBoolean","MERGE",EDGE,{"derivedFrom":[makeQuery(id+"F11.opExtrude","SWEPT_EDGE",EDGE,{"disambiguationData":[OSD([subQ1,subQ0])]}),makeQuery(id+"F12.opExtrude","SWEPT_EDGE",EDGE,{"disambiguationData":[OSD([subQ1,subQ0])]})]});}
            var Q4;
            Q4=makeQuery(id+"F11.opExtrude","CAP_EDGE",EDGE,{"disambiguationData":[OSD([sQuery(id+"F9.wireOp",EDGE,"E36.left")])],"isStart":true});
            var Q5;
            {var subQ0=sQuery(id+"F9.wireOp",EDGE,"E36.top");Q5=makeQuery(id+"F11.boolean.opBoolean","SPLIT",EDGE,{"disambiguationData":[topologyDisambiguationEdgeConnected([makeQuery(id+"F1.opExtrude","CAP_FACE",FACE,{"disambiguationData":[OSD([sQuery(id+"F0.wireOp",EDGE,"E0.bottom"),sQuery(id+"F0.wireOp",EDGE,"E0.top"),sQuery(id+"F0.wireOp",EDGE,"E0.left"),sQuery(id+"F0.wireOp",EDGE,"E0.right"),sQuery(id+"F0.wireOp",EDGE,"E1.filletArc"),sQuery(id+"F0.wireOp",EDGE,"E2.filletArc"),sQuery(id+"F0.wireOp",EDGE,"E3.filletArc"),sQuery(id+"F0.wireOp",EDGE,"E4.filletArc")])],"isStart":false})])],"derivedFrom":makeQuery(id+"F11.opExtrude","CAP_EDGE",EDGE,{"disambiguationData":[OSD([subQ0])],"isStart":true})});}
            var Q6;
            {var subQ0=sQuery(id+"F9.wireOp",EDGE,"E36.bottom");Q6=makeQuery(id+"F11.boolean.opBoolean","SPLIT",EDGE,{"disambiguationData":[topologyDisambiguationEdgeConnected([makeQuery(id+"F1.opExtrude","CAP_FACE",FACE,{"disambiguationData":[OSD([sQuery(id+"F0.wireOp",EDGE,"E0.bottom"),sQuery(id+"F0.wireOp",EDGE,"E0.top"),sQuery(id+"F0.wireOp",EDGE,"E0.left"),sQuery(id+"F0.wireOp",EDGE,"E0.right"),sQuery(id+"F0.wireOp",EDGE,"E1.filletArc"),sQuery(id+"F0.wireOp",EDGE,"E2.filletArc"),sQuery(id+"F0.wireOp",EDGE,"E3.filletArc"),sQuery(id+"F0.wireOp",EDGE,"E4.filletArc")])],"isStart":false})])],"derivedFrom":makeQuery(id+"F11.opExtrude","CAP_EDGE",EDGE,{"disambiguationData":[OSD([subQ0])],"isStart":true})});}
            var Q7;
            Q7=makeQuery(id+"F12.opExtrude","SWEPT_EDGE",EDGE,{"disambiguationData":[OSD([sQuery(id+"F0.wireOp",EDGE,"E0.left"),sQuery(id+"F9.wireOp",EDGE,"E36.bottom")])]});
            var Q8;
            Q8=makeQuery(id+"F12.opExtrude","SWEPT_EDGE",EDGE,{"disambiguationData":[OSD([sQuery(id+"F0.wireOp",EDGE,"E0.left"),sQuery(id+"F9.wireOp",EDGE,"E36.top")])]});
            var Q9;
            Q9=makeQuery(id+"F11.opExtrude","CAP_EDGE",EDGE,{"disambiguationData":[OSD([sQuery(id+"F9.wireOp",EDGE,"E36.left")])],"isStart":false});
            var Q10;
            Q10=makeQuery(id+"F11.opExtrude","SWEPT_EDGE",EDGE,{"disambiguationData":[OSD([sQuery(id+"F9.wireOp",EDGE,"E36.bottom"),sQuery(id+"F9.wireOp",EDGE,"E36.left")])]});
            var Q11;
            Q11=makeQuery(id+"F11.opExtrude","SWEPT_EDGE",EDGE,{"disambiguationData":[OSD([sQuery(id+"F9.wireOp",EDGE,"E36.top"),sQuery(id+"F9.wireOp",EDGE,"E36.left")])]});
            var Q12;
            Q12=makeQuery(id+"F11.opExtrude","CAP_EDGE",EDGE,{"disambiguationData":[OSD([sQuery(id+"F9.wireOp",EDGE,"E36.right")])],"isStart":false});
            var Q13;
            Q13=makeQuery(id+"F17.boolean.opBoolean","COPY",EDGE,{"derivedFrom":makeQuery(id+"F17.opExtrude","CAP_EDGE",EDGE,{"disambiguationData":[OSD([sQuery(id+"F13.wireOp",EDGE,"E38.bottom")])],"isStart":false})});
            var Q14;
            Q14=makeQuery(id+"F17.boolean.opBoolean","COPY",EDGE,{"derivedFrom":makeQuery(id+"F17.opExtrude","CAP_EDGE",EDGE,{"disambiguationData":[OSD([sQuery(id+"F13.wireOp",EDGE,"E38.top")])],"isStart":false})});
            var Q15;
            Q15=makeQuery(id+"F17.boolean.opBoolean","COPY",EDGE,{"derivedFrom":makeQuery(id+"F17.opExtrude","CAP_EDGE",EDGE,{"disambiguationData":[OSD([sQuery(id+"F13.wireOp",EDGE,"E38.left")])],"isStart":false})});
            var Q16;
            Q16=makeQuery(id+"F17.boolean.opBoolean","COPY",EDGE,{"derivedFrom":makeQuery(id+"F17.opExtrude","CAP_EDGE",EDGE,{"disambiguationData":[OSD([sQuery(id+"F13.wireOp",EDGE,"E38.right")])],"isStart":false})});
            var Q17;
            Q17=makeQuery(id+"F16.boolean.opBoolean","COPY",EDGE,{"derivedFrom":makeQuery(id+"F16.opExtrude","CAP_EDGE",EDGE,{"disambiguationData":[OSD([sQuery(id+"F13.wireOp",EDGE,"E38.top")])],"isStart":false})});
            var Q18;
            Q18=makeQuery(id+"F16.boolean.opBoolean","COPY",EDGE,{"derivedFrom":makeQuery(id+"F16.opExtrude","CAP_EDGE",EDGE,{"disambiguationData":[OSD([sQuery(id+"F13.wireOp",EDGE,"E38.left")])],"isStart":false})});
            var Q19;
            Q19=makeQuery(id+"F16.boolean.opBoolean","COPY",EDGE,{"derivedFrom":makeQuery(id+"F16.opExtrude","CAP_EDGE",EDGE,{"disambiguationData":[OSD([sQuery(id+"F13.wireOp",EDGE,"E38.bottom")])],"isStart":false})});
            var Q20;
            Q20=makeQuery(id+"F16.boolean.opBoolean","COPY",EDGE,{"derivedFrom":makeQuery(id+"F16.opExtrude","CAP_EDGE",EDGE,{"disambiguationData":[OSD([sQuery(id+"F13.wireOp",EDGE,"E38.right")])],"isStart":false})});
            fillet(context, id + "F19", {"entities" : qUnion([Q0, Q1, Q2, Q3, Q4, Q5, Q6, Q7, Q8, Q9, Q10, Q11, Q12, Q13, Q14, Q15, Q16, Q17, Q18, Q19, Q20]), "radius" : 2 * mm, "tangentPropagation" : true, "allowEdgeOverflow" : false});
        }
        {
            var Q0;
            Q0=makeQuery(id+"F10.boolean.opBoolean","COPY",EDGE,{"derivedFrom":makeQuery(id+"F10.opExtrude","SWEPT_EDGE",EDGE,{"disambiguationData":[OSD([sQuery(id+"F9.wireOp",EDGE,"E34.bottom"),sQuery(id+"F9.wireOp",EDGE,"E34.left")])]})});
            var Q1;
            Q1=makeQuery(id+"F10.boolean.opBoolean","COPY",EDGE,{"derivedFrom":makeQuery(id+"F10.opExtrude","SWEPT_EDGE",EDGE,{"disambiguationData":[OSD([sQuery(id+"F9.wireOp",EDGE,"E34.bottom"),sQuery(id+"F9.wireOp",EDGE,"E34.right")])]})});
            var Q2;
            Q2=makeQuery(id+"F10.boolean.opBoolean","COPY",EDGE,{"derivedFrom":makeQuery(id+"F10.opExtrude","SWEPT_EDGE",EDGE,{"disambiguationData":[OSD([sQuery(id+"F9.wireOp",EDGE,"E34.top"),sQuery(id+"F9.wireOp",EDGE,"E34.right")])]})});
            var Q3;
            Q3=makeQuery(id+"F10.boolean.opBoolean","COPY",EDGE,{"derivedFrom":makeQuery(id+"F10.opExtrude","SWEPT_EDGE",EDGE,{"disambiguationData":[OSD([sQuery(id+"F9.wireOp",EDGE,"E34.top"),sQuery(id+"F9.wireOp",EDGE,"E34.left")])]})});
            var Q4;
            Q4=makeQuery(id+"F10.boolean.opBoolean","COPY",EDGE,{"derivedFrom":makeQuery(id+"F10.opExtrude","SWEPT_EDGE",EDGE,{"disambiguationData":[OSD([sQuery(id+"F9.wireOp",EDGE,"E35.top"),sQuery(id+"F9.wireOp",EDGE,"E35.right")])]})});
            var Q5;
            Q5=makeQuery(id+"F10.boolean.opBoolean","COPY",EDGE,{"derivedFrom":makeQuery(id+"F10.opExtrude","SWEPT_EDGE",EDGE,{"disambiguationData":[OSD([sQuery(id+"F9.wireOp",EDGE,"E35.top"),sQuery(id+"F9.wireOp",EDGE,"E35.left")])]})});
            var Q6;
            Q6=makeQuery(id+"F10.boolean.opBoolean","COPY",EDGE,{"derivedFrom":makeQuery(id+"F10.opExtrude","SWEPT_EDGE",EDGE,{"disambiguationData":[OSD([sQuery(id+"F9.wireOp",EDGE,"E35.bottom"),sQuery(id+"F9.wireOp",EDGE,"E35.right")])]})});
            var Q7;
            Q7=makeQuery(id+"F10.boolean.opBoolean","COPY",EDGE,{"derivedFrom":makeQuery(id+"F10.opExtrude","SWEPT_EDGE",EDGE,{"disambiguationData":[OSD([sQuery(id+"F9.wireOp",EDGE,"E35.bottom"),sQuery(id+"F9.wireOp",EDGE,"E35.left")])]})});
            fillet(context, id + "F20", {"entities" : qUnion([Q0, Q1, Q2, Q3, Q4, Q5, Q6, Q7]), "radius" : 2 * mm, "tangentPropagation" : true, "allowEdgeOverflow" : false});
        }
    });
